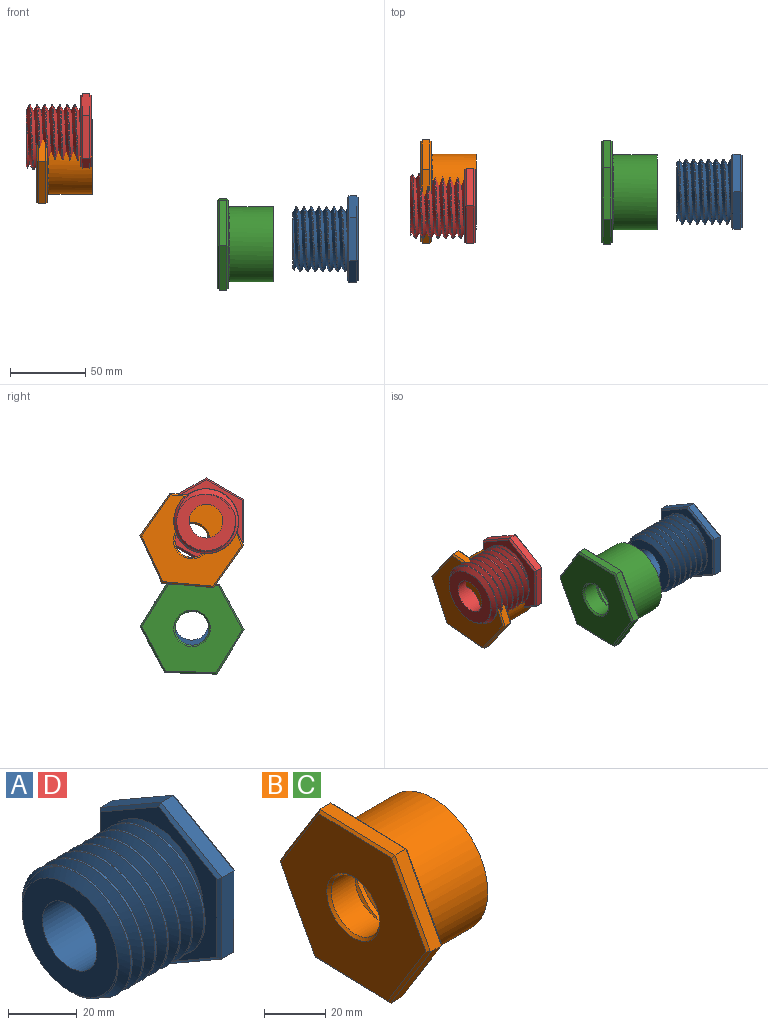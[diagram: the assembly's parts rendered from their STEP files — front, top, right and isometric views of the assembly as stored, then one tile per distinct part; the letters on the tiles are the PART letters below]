
ASSEMBLY  parts=4 mates=1
PART A: 27 faces, bbox 46.3x50.6x58.3 mm
  f0: plane 24.99x14.45mm, normal (0,-0.5,0.87), area 144.3mm2, adj f1,f5,f18,f22
  f1: plane 28.87x5mm, normal (0,-1,0), area 144.3mm2, adj f0,f2,f16,f20
  f2: plane 25.01x14.41mm, normal (0,-0.5,-0.87), area 144.3mm2, adj f1,f3,f14,f19
  f3: plane 24.99x14.45mm, normal (0,0.5,-0.87), area 144.3mm2, adj f2,f4,f13,f21
  f4: plane 28.87x5mm, normal (0,1,0), area 144.3mm2, adj f3,f5,f15,f23
  f5: plane 25.01x14.41mm, normal (0,0.5,0.87), area 144.3mm2, adj f0,f4,f17,f24
  f6: plane 55.43x48.02mm, normal (1,0,0), area 1527.7mm2, adj f13,f14,f15,f16,f17,f18,f26
  f7: plane 55.43x48.02mm, normal (-1,0,0), area 741.4mm2, adj f8,f9,f10,f19,f20,f21,f22,f23
  f8: cylinder r=21.6mm len=43.2mm, axis (1,0,0), area 1076.3mm2, adj f7,f9,f10,f12
  f9: bspline ~49.88x43.2mm, area 3919.9mm2, adj f7,f8,f10,f11,f12
  f10: bspline ~49.88x43.2mm, area 3896.2mm2, adj f7,f8,f9,f11,f12
  f11: plane 39.78x38.04mm, normal (-1,0,0), area 768.6mm2, adj f9,f10,f12,f25
  f12: cone r=21.6mm half-angle=45deg, axis (1,0,0), area 128.1mm2, adj f8,f9,f10,f11
  f13: plane 24.99x15.03mm, normal (0.71,0.35,-0.61), area 40mm2, adj f3,f6,f14,f15
  f14: plane 25.01x14.99mm, normal (0.71,-0.35,-0.61), area 40mm2, adj f2,f6,f13,f16
  f15: plane 28.87x1.02mm, normal (0.71,0.71,0), area 40mm2, adj f4,f6,f13,f17
  f16: plane 28.87x1.02mm, normal (0.71,-0.71,0), area 40mm2, adj f1,f6,f14,f18
  f17: plane 25.01x14.99mm, normal (0.71,0.35,0.61), area 40mm2, adj f5,f6,f15,f18
  f18: plane 24.99x15.03mm, normal (0.71,-0.35,0.61), area 40mm2, adj f0,f6,f16,f17
  f19: plane 25.01x14.99mm, normal (-0.71,-0.35,-0.61), area 40mm2, adj f2,f7,f20,f21
  f20: plane 28.87x1.02mm, normal (-0.71,-0.71,0), area 40mm2, adj f1,f7,f19,f22
  f21: plane 24.99x15.03mm, normal (-0.71,0.35,-0.61), area 40mm2, adj f3,f7,f19,f23
  f22: plane 24.99x15.03mm, normal (-0.71,-0.35,0.61), area 40mm2, adj f0,f7,f20,f24
  f23: plane 28.87x1.02mm, normal (-0.71,0.71,0), area 40mm2, adj f4,f7,f21,f24
  f24: plane 25.01x14.99mm, normal (-0.71,0.35,0.61), area 40mm2, adj f5,f7,f22,f23
  f25: cylinder r=11.2mm len=42.5mm, axis (1,0,0), area 2990.8mm2, adj f11,f26
  f26: cone r=11.2mm half-angle=45deg, axis (1,0,0), area 104mm2, adj f6,f25
PART B: 31 faces, bbox 40.3x70.9x62.6 mm
  f0: cylinder r=20.69mm len=41.39mm, axis (-1,0,0), area 236.4mm2, adj f1,f2,f6,f16
  f1: bspline ~54.29x47.01mm, area 2506.7mm2, adj f0,f2,f3,f5,f16
  f2: bspline ~54.29x47.01mm, area 2507mm2, adj f0,f1,f3,f5,f16
  f3: cylinder r=20.69mm len=41.39mm, axis (1,0,0), area 1144mm2, adj f1,f2,f5,f6
  f4: cylinder r=25mm len=50mm, axis (1,0,0), area 4555.3mm2, adj f5,f17
  f5: plane 51.62x51.62mm, normal (1,0,0), area 494mm2, adj f1,f2,f3,f4
  f6: plane 41.39x41.39mm, normal (1,0,0), area 951.2mm2, adj f0,f3,f15
  f7: plane 66.94x58.99mm, normal (1,0,0), area 789.6mm2, adj f17,f18,f19,f20,f21,f22,f23
  f8: plane 34.63x5mm, normal (0,0.03,-1), area 173.2mm2, adj f9,f13,f23,f30
  f9: plane 29.46x18.22mm, normal (0,-0.85,-0.53), area 173.2mm2, adj f8,f10,f22,f29
  f10: plane 30.51x16.4mm, normal (0,-0.88,0.47), area 173.2mm2, adj f9,f11,f20,f27
  f11: plane 34.63x5mm, normal (0,-0.03,1), area 173.2mm2, adj f10,f12,f18,f25
  f12: plane 29.46x18.22mm, normal (0,0.85,0.53), area 173.2mm2, adj f11,f13,f19,f26
  f13: plane 30.51x16.4mm, normal (0,0.88,-0.47), area 173.2mm2, adj f8,f12,f21,f28
  f14: plane 66.94x58.99mm, normal (-1,0,0), area 2445.7mm2, adj f24,f25,f26,f27,f28,f29,f30
  f15: cylinder r=11.2mm len=22.4mm, axis (-1,0,0), area 774.1mm2, adj f6,f24
  f16: plane 44.37x36.04mm, normal (1,0,0), area 124.1mm2, adj f0,f1,f2
  f17: cone r=25mm half-angle=45deg, axis (-1,0,0), area 226.6mm2, adj f4,f7
  f18: plane 34.63x2.03mm, normal (0.71,-0.02,0.71), area 48.2mm2, adj f7,f11,f19,f20
  f19: plane 29.5x18.77mm, normal (0.71,0.6,0.37), area 48.2mm2, adj f7,f12,f18,f21
  f20: plane 30.51x17.01mm, normal (0.71,-0.62,0.33), area 48.2mm2, adj f7,f10,f18,f22
  f21: plane 30.51x17.01mm, normal (0.71,0.62,-0.33), area 48.2mm2, adj f7,f13,f19,f23
  f22: plane 29.5x18.77mm, normal (0.71,-0.6,-0.37), area 48.2mm2, adj f7,f9,f20,f23
  f23: plane 34.63x2.03mm, normal (0.71,0.02,-0.71), area 48.2mm2, adj f7,f8,f21,f22
  f24: cone r=11.2mm half-angle=45deg, axis (-1,0,0), area 104mm2, adj f14,f15
  f25: plane 34.63x2.03mm, normal (-0.71,-0.02,0.71), area 48.2mm2, adj f11,f14,f26,f27
  f26: plane 29.5x18.77mm, normal (-0.71,0.6,0.37), area 48.2mm2, adj f12,f14,f25,f28
  f27: plane 30.51x17.01mm, normal (-0.71,-0.62,0.33), area 48.2mm2, adj f10,f14,f25,f29
  f28: plane 30.51x17.01mm, normal (-0.71,0.62,-0.33), area 48.2mm2, adj f13,f14,f26,f30
  f29: plane 29.5x18.77mm, normal (-0.71,-0.6,-0.37), area 48.2mm2, adj f9,f14,f27,f30
  f30: plane 34.63x2.03mm, normal (-0.71,0.02,-0.71), area 48.2mm2, adj f8,f14,f28,f29
PART C: same geometry as B
PART D: same geometry as A
PLACE A t=(88.57,-2.99,8.69)mm
PLACE B rot(axis=(1,0,0),123.4deg) t=(-84.9,-3.04,63.83)mm
PLACE C t=(35.65,-3.26,5.32)mm
PLACE D t=(-89.13,-12.63,76.71)mm
MATE cylindrical D.f11 <-> B.f16  axis (-1,0,0) through (-129.13,-12.63,75.76)mm
